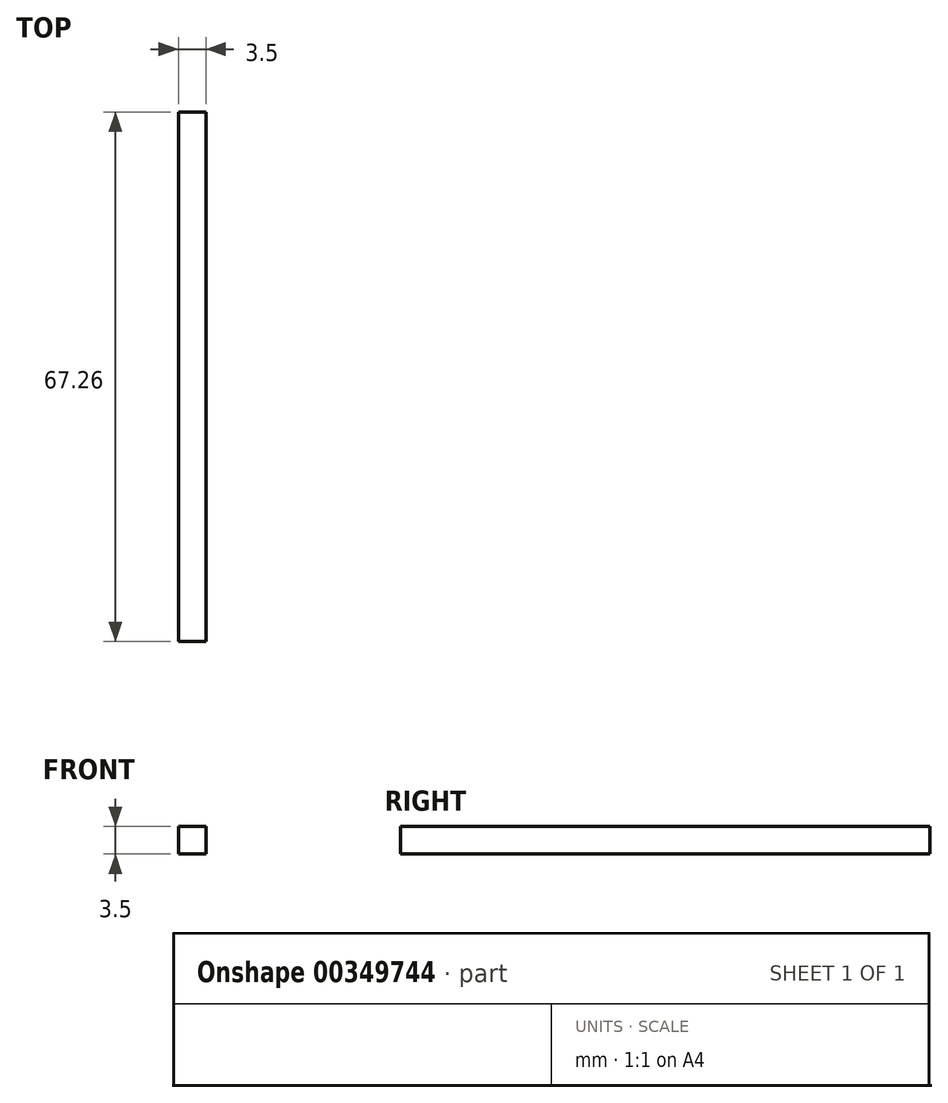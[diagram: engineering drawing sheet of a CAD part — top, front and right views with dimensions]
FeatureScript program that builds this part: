
annotation { "Feature Type Name" : "Feature", "Feature Type Description" : "" }
export const myFeature = defineFeature(function(context is Context, id is Id, definition is map)
    precondition{}
    {
        {
            var Q0;
            Q0=qCreatedBy(makeId("Top.planeOp"),FACE);
            var sketch = newSketch(context, id + "F0", { "sketchPlane" : qUnion([Q0])});
            skLineSegment(sketch, "E0.bottom", {"start": v(1.75, -33.64) * mm, "end": v(-1.75, -33.64) * mm});
            skLineSegment(sketch, "E0.top", {"start": v(1.75, 33.64) * mm, "end": v(-1.75, 33.64) * mm});
            skLineSegment(sketch, "E0.left", {"start": v(1.75, -33.64) * mm, "end": v(1.75, 33.63) * mm});
            skLineSegment(sketch, "E0.right", {"start": v(-1.75, -33.64) * mm, "end": v(-1.75, 33.63) * mm});
            skPoint(sketch, "E0.middle", {"position": v(0, 0) * mm});
            skSolve(sketch);
        }
        {
            var Q0;
            Q0=qSketchRegion(id+"F0",true);
            extrude(context, id + "F1", {"entities" : qUnion([Q0]), "depth" : 3.5 * mm});
        }
    });
